# Revit family: RAIL XDTP6
name_source: partatom
category: Luminarias
units: mm (PartAtom-declared; Revit-internal decimal feet)

## family parameters
Compartido = Sí
Corte con vacíos al cargar = No
Cota de conector redondo = Diámetro de uso
Origen de luz = No
Punto de cálculo de habitación = No
Se basa en plano de trabajo = Sí
Siempre vertical = No
Tipo de pieza = Normal

## types (4) — shared parameters
Elevación por defecto = 1219 mm
Fabricante = BRILLANT
zero-valued in all types: XDTFP.2

## per-type parameters (varying)
| type | Descripción | Longitud | Modelo | XDTFP.1 | XDTTF.1 |
| RIEL_XDTP61.1 | RIEL DE 6 ENTRADAS Y 3 CIRCUITOS, IP20, ACABADO EN COLOR NEGRO POR STOCK (OPCION A BLANCO, POR PROYECTO). LONGITUD DE 1M | 1000 mm  [stored 3.28084 ft] | XDTP61.1 | 1 | 1 |
| RIEL_XDTP615.1 | RIEL DE 6 ENTRADAS Y 3 CIRCUITOS, IP20, ACABADO EN COLOR NEGRO POR STOCK (OPCION A BLANCO, POR PROYECTO). LONGITUD DE 1.5M | 1500 mm | XDTP615.1 | 0 | 0 |
| RIEL_XDTP62.1 | RIEL DE 6 ENTRADAS Y 3 CIRCUITOS, IP20, ACABADO EN COLOR NEGRO POR STOCK (OPCION A BLANCO, POR PROYECTO). LONGITUD DE 2M | 2000 mm | XDTP62.1 | 0 | 0 |
| RIEL_XDTP63.1 | RIEL DE 6 ENTRADAS Y 3 CIRCUITOS, IP20, ACABADO EN COLOR NEGRO POR STOCK (OPCION A BLANCO, POR PROYECTO). LONGITUD DE 3M | 3000 mm | XDTP63.1 | 0 | 0 |

note: [stored X ft] marks values corroborated as IEEE doubles in the binary element streams (Revit-internal decimal feet)

## geometry (parser evidence)
native form markers: Blend x2
no freeform markers — native parametric forms only
